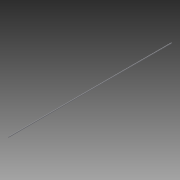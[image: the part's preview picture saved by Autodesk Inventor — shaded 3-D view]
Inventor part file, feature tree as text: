
AUTODESK INVENTOR PART (.ipt)
format: ipt  version: 2014 SP1 (Build 180222100, 222)  size: 63,488 bytes
history: native  units: in
note: dims shown in document units (in); Inventor stores cm internally (conversion verified against a paired STEP export)
features: extrude x1, sketch x1
ambient origin geometry x8: Origin, YZ Plane, XZ Plane, XY Plane, X Axis, Y Axis, Z Axis, Center Point
bodies: Solid1 (feature_tree)
feature tree (2):
  extrude  "Extrusion1"  Depth=50.0in TaperAngle=0.0deg
  sketch  "Sketch1"  dims[d0=0.25in d1=50.0in d2=0.0in]
